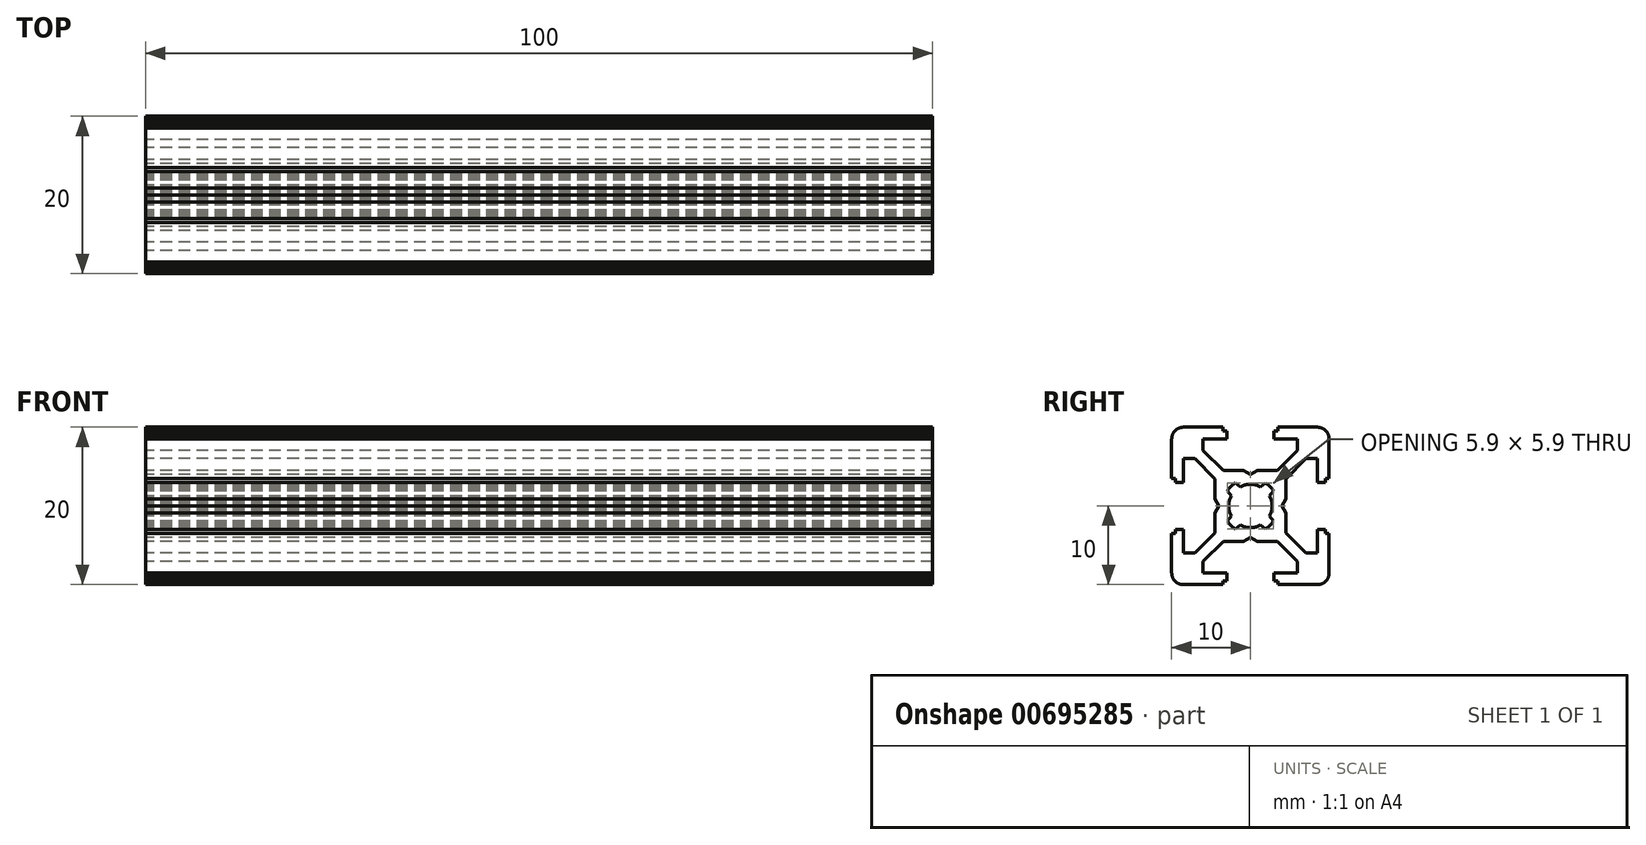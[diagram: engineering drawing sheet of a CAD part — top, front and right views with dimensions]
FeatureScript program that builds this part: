
annotation { "Feature Type Name" : "Feature", "Feature Type Description" : "" }
export const myFeature = defineFeature(function(context is Context, id is Id, definition is map)
    precondition{}
    {
        {
            var Q0;
            Q0=qCreatedBy(makeId("Right.planeOp"),FACE);
            var sketch = newSketch(context, id + "F0", { "sketchPlane" : qUnion([Q0])});
            skLineSegment(sketch, "E0", {"start": v(-10, -8.57) * mm, "end": v(-10, -8.5) * mm});
            skLineSegment(sketch, "E1", {"start": v(10, 8.5) * mm, "end": v(10, 8.57) * mm});
            skLineSegment(sketch, "E2", {"start": v(-2.74, -0.2) * mm, "end": v(-2.75, -0.07) * mm});
            skLineSegment(sketch, "E3", {"start": v(2.75, 0.07) * mm, "end": v(2.74, 0.2) * mm});
            skLineSegment(sketch, "E4", {"start": v(-10, -8.63) * mm, "end": v(-10, -8.57) * mm});
            skLineSegment(sketch, "E5", {"start": v(10, 8.57) * mm, "end": v(10, 8.63) * mm});
            skLineSegment(sketch, "E6", {"start": v(-2.73, -0.35) * mm, "end": v(-2.74, -0.2) * mm});
            skLineSegment(sketch, "E7", {"start": v(2.74, 0.2) * mm, "end": v(2.73, 0.35) * mm});
            skLineSegment(sketch, "E8", {"start": v(-9.99, -8.7) * mm, "end": v(-10, -8.63) * mm});
            skLineSegment(sketch, "E9", {"start": v(10, 8.63) * mm, "end": v(9.99, 8.7) * mm});
            skLineSegment(sketch, "E10", {"start": v(-2.7, -0.49) * mm, "end": v(-2.73, -0.35) * mm});
            skLineSegment(sketch, "E11", {"start": v(2.73, 0.35) * mm, "end": v(2.7, 0.49) * mm});
            skLineSegment(sketch, "E12", {"start": v(-9.98, -8.77) * mm, "end": v(-9.99, -8.7) * mm});
            skLineSegment(sketch, "E13", {"start": v(9.99, 8.7) * mm, "end": v(9.98, 8.77) * mm});
            skLineSegment(sketch, "E14", {"start": v(-9.96, -8.83) * mm, "end": v(-9.98, -8.77) * mm});
            skLineSegment(sketch, "E15", {"start": v(9.98, 8.77) * mm, "end": v(9.96, 8.83) * mm});
            skLineSegment(sketch, "E16", {"start": v(-2.68, -0.62) * mm, "end": v(-2.7, -0.49) * mm});
            skLineSegment(sketch, "E17", {"start": v(2.7, 0.49) * mm, "end": v(2.68, 0.62) * mm});
            skLineSegment(sketch, "E18", {"start": v(-9.95, -8.9) * mm, "end": v(-9.96, -8.83) * mm});
            skLineSegment(sketch, "E19", {"start": v(9.96, 8.83) * mm, "end": v(9.95, 8.9) * mm});
            skLineSegment(sketch, "E20", {"start": v(-2.64, -0.76) * mm, "end": v(-2.68, -0.62) * mm});
            skLineSegment(sketch, "E21", {"start": v(2.68, 0.62) * mm, "end": v(2.64, 0.76) * mm});
            skLineSegment(sketch, "E22", {"start": v(-9.93, -8.96) * mm, "end": v(-9.95, -8.9) * mm});
            skLineSegment(sketch, "E23", {"start": v(9.95, 8.9) * mm, "end": v(9.93, 8.96) * mm});
            skLineSegment(sketch, "E24", {"start": v(-2.6, -0.9) * mm, "end": v(-2.64, -0.76) * mm});
            skLineSegment(sketch, "E25", {"start": v(2.64, 0.76) * mm, "end": v(2.6, 0.9) * mm});
            skLineSegment(sketch, "E26", {"start": v(-9.9, -9.03) * mm, "end": v(-9.93, -8.96) * mm});
            skLineSegment(sketch, "E27", {"start": v(9.93, 8.96) * mm, "end": v(9.9, 9.03) * mm});
            skLineSegment(sketch, "E28", {"start": v(-2.55, -1.02) * mm, "end": v(-2.6, -0.9) * mm});
            skLineSegment(sketch, "E29", {"start": v(2.6, 0.9) * mm, "end": v(2.55, 1.02) * mm});
            skLineSegment(sketch, "E30", {"start": v(-9.88, -9.09) * mm, "end": v(-9.9, -9.03) * mm});
            skLineSegment(sketch, "E31", {"start": v(9.9, 9.03) * mm, "end": v(9.88, 9.09) * mm});
            skLineSegment(sketch, "E32", {"start": v(-2.5, -1.15) * mm, "end": v(-2.55, -1.02) * mm});
            skLineSegment(sketch, "E33", {"start": v(2.55, 1.02) * mm, "end": v(2.5, 1.15) * mm});
            skLineSegment(sketch, "E34", {"start": v(-9.85, -9.15) * mm, "end": v(-9.88, -9.09) * mm});
            skLineSegment(sketch, "E35", {"start": v(9.88, 9.09) * mm, "end": v(9.85, 9.15) * mm});
            skLineSegment(sketch, "E36", {"start": v(-2.44, -1.28) * mm, "end": v(-2.5, -1.15) * mm});
            skLineSegment(sketch, "E37", {"start": v(2.5, 1.15) * mm, "end": v(2.44, 1.28) * mm});
            skLineSegment(sketch, "E38", {"start": v(-9.82, -9.21) * mm, "end": v(-9.85, -9.15) * mm});
            skLineSegment(sketch, "E39", {"start": v(9.85, 9.15) * mm, "end": v(9.82, 9.21) * mm});
            skLineSegment(sketch, "E40", {"start": v(-9.79, -9.27) * mm, "end": v(-9.82, -9.21) * mm});
            skLineSegment(sketch, "E41", {"start": v(9.82, 9.21) * mm, "end": v(9.79, 9.27) * mm});
            skLineSegment(sketch, "E42", {"start": v(4.5, -0.87) * mm, "end": v(4, 0) * mm});
            skLineSegment(sketch, "E43", {"start": v(-4, 0) * mm, "end": v(-4.5, 0.87) * mm});
            skLineSegment(sketch, "E44", {"start": v(-9.75, -9.33) * mm, "end": v(-9.79, -9.27) * mm});
            skLineSegment(sketch, "E45", {"start": v(9.79, 9.27) * mm, "end": v(9.75, 9.33) * mm});
            skLineSegment(sketch, "E46", {"start": v(-2.87, -2) * mm, "end": v(-2.95, -1.89) * mm});
            skLineSegment(sketch, "E47", {"start": v(2.95, 1.89) * mm, "end": v(2.87, 2) * mm});
            skLineSegment(sketch, "E48", {"start": v(-9.71, -9.38) * mm, "end": v(-9.75, -9.33) * mm});
            skLineSegment(sketch, "E49", {"start": v(9.75, 9.33) * mm, "end": v(9.71, 9.38) * mm});
            skLineSegment(sketch, "E50", {"start": v(-2.8, -2.11) * mm, "end": v(-2.87, -2) * mm});
            skLineSegment(sketch, "E51", {"start": v(2.87, 2) * mm, "end": v(2.8, 2.11) * mm});
            skLineSegment(sketch, "E52", {"start": v(-9.67, -9.44) * mm, "end": v(-9.71, -9.38) * mm});
            skLineSegment(sketch, "E53", {"start": v(9.71, 9.38) * mm, "end": v(9.67, 9.44) * mm});
            skLineSegment(sketch, "E54", {"start": v(-2.7, -2.22) * mm, "end": v(-2.8, -2.11) * mm});
            skLineSegment(sketch, "E55", {"start": v(2.8, 2.11) * mm, "end": v(2.7, 2.22) * mm});
            skLineSegment(sketch, "E56", {"start": v(-9.63, -9.49) * mm, "end": v(-9.67, -9.44) * mm});
            skLineSegment(sketch, "E57", {"start": v(9.67, 9.44) * mm, "end": v(9.63, 9.49) * mm});
            skLineSegment(sketch, "E58", {"start": v(2.95, -1.89) * mm, "end": v(2.44, -1.28) * mm});
            skLineSegment(sketch, "E59", {"start": v(-2.44, 1.28) * mm, "end": v(-2.95, 1.89) * mm});
            skLineSegment(sketch, "E60", {"start": v(-2.62, -2.32) * mm, "end": v(-2.7, -2.22) * mm});
            skLineSegment(sketch, "E61", {"start": v(2.7, 2.22) * mm, "end": v(2.62, 2.32) * mm});
            skLineSegment(sketch, "E62", {"start": v(-9.58, -9.54) * mm, "end": v(-9.63, -9.49) * mm});
            skLineSegment(sketch, "E63", {"start": v(9.63, 9.49) * mm, "end": v(9.58, 9.54) * mm});
            skLineSegment(sketch, "E64", {"start": v(-2.52, -2.43) * mm, "end": v(-2.62, -2.32) * mm});
            skLineSegment(sketch, "E65", {"start": v(2.62, 2.32) * mm, "end": v(2.52, 2.43) * mm});
            skLineSegment(sketch, "E66", {"start": v(-2.43, -2.52) * mm, "end": v(-2.52, -2.43) * mm});
            skLineSegment(sketch, "E67", {"start": v(2.52, 2.43) * mm, "end": v(2.43, 2.52) * mm});
            skLineSegment(sketch, "E68", {"start": v(-9.54, -9.58) * mm, "end": v(-9.58, -9.54) * mm});
            skLineSegment(sketch, "E69", {"start": v(7.06, -6) * mm, "end": v(4.5, -3.44) * mm});
            skLineSegment(sketch, "E70", {"start": v(-4.5, 3.44) * mm, "end": v(-7.06, 6) * mm});
            skLineSegment(sketch, "E71", {"start": v(6, -7.06) * mm, "end": v(3.44, -4.5) * mm});
            skLineSegment(sketch, "E72", {"start": v(-3.44, 4.5) * mm, "end": v(-6, 7.06) * mm});
            skLineSegment(sketch, "E73", {"start": v(9.58, 9.54) * mm, "end": v(9.54, 9.58) * mm});
            skLineSegment(sketch, "E74", {"start": v(-2.32, -2.62) * mm, "end": v(-2.43, -2.52) * mm});
            skLineSegment(sketch, "E75", {"start": v(2.43, 2.52) * mm, "end": v(2.32, 2.62) * mm});
            skLineSegment(sketch, "E76", {"start": v(-9.49, -9.63) * mm, "end": v(-9.54, -9.58) * mm});
            skLineSegment(sketch, "E77", {"start": v(9.54, 9.58) * mm, "end": v(9.49, 9.63) * mm});
            skLineSegment(sketch, "E78", {"start": v(-2.22, -2.7) * mm, "end": v(-2.32, -2.62) * mm});
            skLineSegment(sketch, "E79", {"start": v(2.32, 2.62) * mm, "end": v(2.22, 2.7) * mm});
            skLineSegment(sketch, "E80", {"start": v(1.89, -2.95) * mm, "end": v(1.28, -2.44) * mm});
            skLineSegment(sketch, "E81", {"start": v(-1.28, 2.44) * mm, "end": v(-1.89, 2.95) * mm});
            skLineSegment(sketch, "E82", {"start": v(-9.44, -9.67) * mm, "end": v(-9.49, -9.63) * mm});
            skLineSegment(sketch, "E83", {"start": v(9.49, 9.63) * mm, "end": v(9.44, 9.67) * mm});
            skLineSegment(sketch, "E84", {"start": v(-2.11, -2.8) * mm, "end": v(-2.22, -2.7) * mm});
            skLineSegment(sketch, "E85", {"start": v(2.22, 2.7) * mm, "end": v(2.11, 2.8) * mm});
            skLineSegment(sketch, "E86", {"start": v(-9.38, -9.71) * mm, "end": v(-9.44, -9.67) * mm});
            skLineSegment(sketch, "E87", {"start": v(9.44, 9.67) * mm, "end": v(9.38, 9.71) * mm});
            skLineSegment(sketch, "E88", {"start": v(-2, -2.87) * mm, "end": v(-2.11, -2.8) * mm});
            skLineSegment(sketch, "E89", {"start": v(2.11, 2.8) * mm, "end": v(2, 2.87) * mm});
            skLineSegment(sketch, "E90", {"start": v(-9.33, -9.75) * mm, "end": v(-9.38, -9.71) * mm});
            skLineSegment(sketch, "E91", {"start": v(9.38, 9.71) * mm, "end": v(9.33, 9.75) * mm});
            skLineSegment(sketch, "E92", {"start": v(-1.89, -2.95) * mm, "end": v(-2, -2.87) * mm});
            skLineSegment(sketch, "E93", {"start": v(2, 2.87) * mm, "end": v(1.89, 2.95) * mm});
            skLineSegment(sketch, "E94", {"start": v(-9.27, -9.79) * mm, "end": v(-9.33, -9.75) * mm});
            skLineSegment(sketch, "E95", {"start": v(9.33, 9.75) * mm, "end": v(9.27, 9.79) * mm});
            skLineSegment(sketch, "E96", {"start": v(0.87, -4.5) * mm, "end": v(0, -4) * mm});
            skLineSegment(sketch, "E97", {"start": v(0, 4) * mm, "end": v(-0.87, 4.5) * mm});
            skLineSegment(sketch, "E98", {"start": v(-9.21, -9.82) * mm, "end": v(-9.27, -9.79) * mm});
            skLineSegment(sketch, "E99", {"start": v(9.27, 9.79) * mm, "end": v(9.21, 9.82) * mm});
            skLineSegment(sketch, "E100", {"start": v(-9.15, -9.85) * mm, "end": v(-9.21, -9.82) * mm});
            skLineSegment(sketch, "E101", {"start": v(9.21, 9.82) * mm, "end": v(9.15, 9.85) * mm});
            skLineSegment(sketch, "E102", {"start": v(-1.15, -2.5) * mm, "end": v(-1.28, -2.44) * mm});
            skLineSegment(sketch, "E103", {"start": v(1.28, 2.44) * mm, "end": v(1.15, 2.5) * mm});
            skLineSegment(sketch, "E104", {"start": v(-9.09, -9.88) * mm, "end": v(-9.15, -9.85) * mm});
            skLineSegment(sketch, "E105", {"start": v(9.15, 9.85) * mm, "end": v(9.09, 9.88) * mm});
            skLineSegment(sketch, "E106", {"start": v(-1.02, -2.55) * mm, "end": v(-1.15, -2.5) * mm});
            skLineSegment(sketch, "E107", {"start": v(1.15, 2.5) * mm, "end": v(1.02, 2.55) * mm});
            skLineSegment(sketch, "E108", {"start": v(-9.03, -9.9) * mm, "end": v(-9.09, -9.88) * mm});
            skLineSegment(sketch, "E109", {"start": v(9.09, 9.88) * mm, "end": v(9.03, 9.9) * mm});
            skLineSegment(sketch, "E110", {"start": v(-0.9, -2.6) * mm, "end": v(-1.02, -2.55) * mm});
            skLineSegment(sketch, "E111", {"start": v(1.02, 2.55) * mm, "end": v(0.9, 2.6) * mm});
            skLineSegment(sketch, "E112", {"start": v(-8.96, -9.93) * mm, "end": v(-9.03, -9.9) * mm});
            skLineSegment(sketch, "E113", {"start": v(9.03, 9.9) * mm, "end": v(8.96, 9.93) * mm});
            skLineSegment(sketch, "E114", {"start": v(-0.76, -2.64) * mm, "end": v(-0.9, -2.6) * mm});
            skLineSegment(sketch, "E115", {"start": v(0.9, 2.6) * mm, "end": v(0.76, 2.64) * mm});
            skLineSegment(sketch, "E116", {"start": v(-8.9, -9.95) * mm, "end": v(-8.96, -9.93) * mm});
            skLineSegment(sketch, "E117", {"start": v(8.96, 9.93) * mm, "end": v(8.9, 9.95) * mm});
            skLineSegment(sketch, "E118", {"start": v(-0.62, -2.68) * mm, "end": v(-0.76, -2.64) * mm});
            skLineSegment(sketch, "E119", {"start": v(0.76, 2.64) * mm, "end": v(0.62, 2.68) * mm});
            skLineSegment(sketch, "E120", {"start": v(-8.83, -9.96) * mm, "end": v(-8.9, -9.95) * mm});
            skLineSegment(sketch, "E121", {"start": v(8.9, 9.95) * mm, "end": v(8.83, 9.96) * mm});
            skLineSegment(sketch, "E122", {"start": v(-0.49, -2.7) * mm, "end": v(-0.62, -2.68) * mm});
            skLineSegment(sketch, "E123", {"start": v(0.62, 2.68) * mm, "end": v(0.49, 2.7) * mm});
            skLineSegment(sketch, "E124", {"start": v(-8.77, -9.98) * mm, "end": v(-8.83, -9.96) * mm});
            skLineSegment(sketch, "E125", {"start": v(8.83, 9.96) * mm, "end": v(8.77, 9.98) * mm});
            skLineSegment(sketch, "E126", {"start": v(-8.7, -9.99) * mm, "end": v(-8.77, -9.98) * mm});
            skLineSegment(sketch, "E127", {"start": v(8.77, 9.98) * mm, "end": v(8.7, 9.99) * mm});
            skLineSegment(sketch, "E128", {"start": v(-0.35, -2.73) * mm, "end": v(-0.49, -2.7) * mm});
            skLineSegment(sketch, "E129", {"start": v(0.49, 2.7) * mm, "end": v(0.35, 2.73) * mm});
            skLineSegment(sketch, "E130", {"start": v(-8.63, -10) * mm, "end": v(-8.7, -9.99) * mm});
            skLineSegment(sketch, "E131", {"start": v(8.7, 9.99) * mm, "end": v(8.63, 10) * mm});
            skLineSegment(sketch, "E132", {"start": v(-0.2, -2.74) * mm, "end": v(-0.35, -2.73) * mm});
            skLineSegment(sketch, "E133", {"start": v(0.35, 2.73) * mm, "end": v(0.2, 2.74) * mm});
            skLineSegment(sketch, "E134", {"start": v(-8.57, -10) * mm, "end": v(-8.63, -10) * mm});
            skLineSegment(sketch, "E135", {"start": v(8.63, 10) * mm, "end": v(8.57, 10) * mm});
            skLineSegment(sketch, "E136", {"start": v(-0.07, -2.75) * mm, "end": v(-0.2, -2.74) * mm});
            skLineSegment(sketch, "E137", {"start": v(0.2, 2.74) * mm, "end": v(0.07, 2.75) * mm});
            skLineSegment(sketch, "E138", {"start": v(-8.5, -10) * mm, "end": v(-8.57, -10) * mm});
            skLineSegment(sketch, "E139", {"start": v(8.57, 10) * mm, "end": v(8.5, 10) * mm});
            skLineSegment(sketch, "E140", {"start": v(-8.5, -10) * mm, "end": v(-3.5, -10) * mm});
            skLineSegment(sketch, "E141", {"start": v(3.5, -10) * mm, "end": v(8.5, -10) * mm});
            skLineSegment(sketch, "E142", {"start": v(-3.5, -9.5) * mm, "end": v(-3, -9.5) * mm});
            skLineSegment(sketch, "E143", {"start": v(3, -9.5) * mm, "end": v(3.5, -9.5) * mm});
            skLineSegment(sketch, "E144", {"start": v(-6, -8.5) * mm, "end": v(-3, -8.5) * mm});
            skLineSegment(sketch, "E145", {"start": v(3, -8.5) * mm, "end": v(6, -8.5) * mm});
            skLineSegment(sketch, "E146", {"start": v(-8.5, -6) * mm, "end": v(-7.06, -6) * mm});
            skLineSegment(sketch, "E147", {"start": v(7.06, -6) * mm, "end": v(8.5, -6) * mm});
            skLineSegment(sketch, "E148", {"start": v(-3.44, -4.5) * mm, "end": v(-0.87, -4.5) * mm});
            skLineSegment(sketch, "E149", {"start": v(0.87, -4.5) * mm, "end": v(3.44, -4.5) * mm});
            skLineSegment(sketch, "E150", {"start": v(-10, -3.5) * mm, "end": v(-9.5, -3.5) * mm});
            skLineSegment(sketch, "E151", {"start": v(9.5, -3.5) * mm, "end": v(10, -3.5) * mm});
            skLineSegment(sketch, "E152", {"start": v(-9.5, -3) * mm, "end": v(-8.5, -3) * mm});
            skLineSegment(sketch, "E153", {"start": v(8.5, -3) * mm, "end": v(9.5, -3) * mm});
            skLineSegment(sketch, "E154", {"start": v(-0.07, -2.75) * mm, "end": v(0.07, -2.75) * mm});
            skLineSegment(sketch, "E155", {"start": v(-0.07, 2.75) * mm, "end": v(0.07, 2.75) * mm});
            skLineSegment(sketch, "E156", {"start": v(8.5, 3) * mm, "end": v(9.5, 3) * mm});
            skLineSegment(sketch, "E157", {"start": v(-9.5, 3) * mm, "end": v(-8.5, 3) * mm});
            skLineSegment(sketch, "E158", {"start": v(9.5, 3.5) * mm, "end": v(10, 3.5) * mm});
            skLineSegment(sketch, "E159", {"start": v(-10, 3.5) * mm, "end": v(-9.5, 3.5) * mm});
            skLineSegment(sketch, "E160", {"start": v(0.87, 4.5) * mm, "end": v(3.44, 4.5) * mm});
            skLineSegment(sketch, "E161", {"start": v(-3.44, 4.5) * mm, "end": v(-0.87, 4.5) * mm});
            skLineSegment(sketch, "E162", {"start": v(7.06, 6) * mm, "end": v(8.5, 6) * mm});
            skLineSegment(sketch, "E163", {"start": v(-8.5, 6) * mm, "end": v(-7.06, 6) * mm});
            skLineSegment(sketch, "E164", {"start": v(3, 8.5) * mm, "end": v(6, 8.5) * mm});
            skLineSegment(sketch, "E165", {"start": v(-6, 8.5) * mm, "end": v(-3, 8.5) * mm});
            skLineSegment(sketch, "E166", {"start": v(3, 9.5) * mm, "end": v(3.5, 9.5) * mm});
            skLineSegment(sketch, "E167", {"start": v(-3.5, 9.5) * mm, "end": v(-3, 9.5) * mm});
            skLineSegment(sketch, "E168", {"start": v(3.5, 10) * mm, "end": v(8.5, 10) * mm});
            skLineSegment(sketch, "E169", {"start": v(-8.5, 10) * mm, "end": v(-3.5, 10) * mm});
            skLineSegment(sketch, "E170", {"start": v(8.5, -10) * mm, "end": v(8.57, -10) * mm});
            skLineSegment(sketch, "E171", {"start": v(-8.57, 10) * mm, "end": v(-8.5, 10) * mm});
            skLineSegment(sketch, "E172", {"start": v(0.07, -2.75) * mm, "end": v(0.2, -2.74) * mm});
            skLineSegment(sketch, "E173", {"start": v(-0.2, 2.74) * mm, "end": v(-0.07, 2.75) * mm});
            skLineSegment(sketch, "E174", {"start": v(8.57, -10) * mm, "end": v(8.63, -10) * mm});
            skLineSegment(sketch, "E175", {"start": v(-8.63, 10) * mm, "end": v(-8.57, 10) * mm});
            skLineSegment(sketch, "E176", {"start": v(0.2, -2.74) * mm, "end": v(0.35, -2.73) * mm});
            skLineSegment(sketch, "E177", {"start": v(-0.35, 2.73) * mm, "end": v(-0.2, 2.74) * mm});
            skLineSegment(sketch, "E178", {"start": v(8.63, -10) * mm, "end": v(8.7, -9.99) * mm});
            skLineSegment(sketch, "E179", {"start": v(-8.7, 9.99) * mm, "end": v(-8.63, 10) * mm});
            skLineSegment(sketch, "E180", {"start": v(0.35, -2.73) * mm, "end": v(0.49, -2.7) * mm});
            skLineSegment(sketch, "E181", {"start": v(-0.49, 2.7) * mm, "end": v(-0.35, 2.73) * mm});
            skLineSegment(sketch, "E182", {"start": v(8.7, -9.99) * mm, "end": v(8.77, -9.98) * mm});
            skLineSegment(sketch, "E183", {"start": v(-8.77, 9.98) * mm, "end": v(-8.7, 9.99) * mm});
            skLineSegment(sketch, "E184", {"start": v(8.77, -9.98) * mm, "end": v(8.83, -9.96) * mm});
            skLineSegment(sketch, "E185", {"start": v(-8.83, 9.96) * mm, "end": v(-8.77, 9.98) * mm});
            skLineSegment(sketch, "E186", {"start": v(0.49, -2.7) * mm, "end": v(0.62, -2.68) * mm});
            skLineSegment(sketch, "E187", {"start": v(-0.62, 2.68) * mm, "end": v(-0.49, 2.7) * mm});
            skLineSegment(sketch, "E188", {"start": v(8.83, -9.96) * mm, "end": v(8.9, -9.95) * mm});
            skLineSegment(sketch, "E189", {"start": v(-8.9, 9.95) * mm, "end": v(-8.83, 9.96) * mm});
            skLineSegment(sketch, "E190", {"start": v(0.62, -2.68) * mm, "end": v(0.76, -2.64) * mm});
            skLineSegment(sketch, "E191", {"start": v(-0.76, 2.64) * mm, "end": v(-0.62, 2.68) * mm});
            skLineSegment(sketch, "E192", {"start": v(8.9, -9.95) * mm, "end": v(8.96, -9.93) * mm});
            skLineSegment(sketch, "E193", {"start": v(-8.96, 9.93) * mm, "end": v(-8.9, 9.95) * mm});
            skLineSegment(sketch, "E194", {"start": v(0.76, -2.64) * mm, "end": v(0.9, -2.6) * mm});
            skLineSegment(sketch, "E195", {"start": v(-0.9, 2.6) * mm, "end": v(-0.76, 2.64) * mm});
            skLineSegment(sketch, "E196", {"start": v(8.96, -9.93) * mm, "end": v(9.03, -9.9) * mm});
            skLineSegment(sketch, "E197", {"start": v(-9.03, 9.9) * mm, "end": v(-8.96, 9.93) * mm});
            skLineSegment(sketch, "E198", {"start": v(0.9, -2.6) * mm, "end": v(1.02, -2.55) * mm});
            skLineSegment(sketch, "E199", {"start": v(-1.02, 2.55) * mm, "end": v(-0.9, 2.6) * mm});
            skLineSegment(sketch, "E200", {"start": v(9.03, -9.9) * mm, "end": v(9.09, -9.88) * mm});
            skLineSegment(sketch, "E201", {"start": v(-9.09, 9.88) * mm, "end": v(-9.03, 9.9) * mm});
            skLineSegment(sketch, "E202", {"start": v(1.02, -2.55) * mm, "end": v(1.15, -2.5) * mm});
            skLineSegment(sketch, "E203", {"start": v(-1.15, 2.5) * mm, "end": v(-1.02, 2.55) * mm});
            skLineSegment(sketch, "E204", {"start": v(9.09, -9.88) * mm, "end": v(9.15, -9.85) * mm});
            skLineSegment(sketch, "E205", {"start": v(-9.15, 9.85) * mm, "end": v(-9.09, 9.88) * mm});
            skLineSegment(sketch, "E206", {"start": v(1.15, -2.5) * mm, "end": v(1.28, -2.44) * mm});
            skLineSegment(sketch, "E207", {"start": v(-1.28, 2.44) * mm, "end": v(-1.15, 2.5) * mm});
            skLineSegment(sketch, "E208", {"start": v(9.15, -9.85) * mm, "end": v(9.21, -9.82) * mm});
            skLineSegment(sketch, "E209", {"start": v(-9.21, 9.82) * mm, "end": v(-9.15, 9.85) * mm});
            skLineSegment(sketch, "E210", {"start": v(9.21, -9.82) * mm, "end": v(9.27, -9.79) * mm});
            skLineSegment(sketch, "E211", {"start": v(-9.27, 9.79) * mm, "end": v(-9.21, 9.82) * mm});
            skLineSegment(sketch, "E212", {"start": v(-0.87, -4.5) * mm, "end": v(0, -4) * mm});
            skLineSegment(sketch, "E213", {"start": v(0, 4) * mm, "end": v(0.87, 4.5) * mm});
            skLineSegment(sketch, "E214", {"start": v(9.27, -9.79) * mm, "end": v(9.33, -9.75) * mm});
            skLineSegment(sketch, "E215", {"start": v(-9.33, 9.75) * mm, "end": v(-9.27, 9.79) * mm});
            skLineSegment(sketch, "E216", {"start": v(1.89, -2.95) * mm, "end": v(2, -2.87) * mm});
            skLineSegment(sketch, "E217", {"start": v(-2, 2.87) * mm, "end": v(-1.89, 2.95) * mm});
            skLineSegment(sketch, "E218", {"start": v(9.33, -9.75) * mm, "end": v(9.38, -9.71) * mm});
            skLineSegment(sketch, "E219", {"start": v(-9.38, 9.71) * mm, "end": v(-9.33, 9.75) * mm});
            skLineSegment(sketch, "E220", {"start": v(2, -2.87) * mm, "end": v(2.11, -2.8) * mm});
            skLineSegment(sketch, "E221", {"start": v(-2.11, 2.8) * mm, "end": v(-2, 2.87) * mm});
            skLineSegment(sketch, "E222", {"start": v(9.38, -9.71) * mm, "end": v(9.44, -9.67) * mm});
            skLineSegment(sketch, "E223", {"start": v(-9.44, 9.67) * mm, "end": v(-9.38, 9.71) * mm});
            skLineSegment(sketch, "E224", {"start": v(2.11, -2.8) * mm, "end": v(2.22, -2.7) * mm});
            skLineSegment(sketch, "E225", {"start": v(-2.22, 2.7) * mm, "end": v(-2.11, 2.8) * mm});
            skLineSegment(sketch, "E226", {"start": v(9.44, -9.67) * mm, "end": v(9.49, -9.63) * mm});
            skLineSegment(sketch, "E227", {"start": v(-9.49, 9.63) * mm, "end": v(-9.44, 9.67) * mm});
            skLineSegment(sketch, "E228", {"start": v(-1.89, -2.95) * mm, "end": v(-1.28, -2.44) * mm});
            skLineSegment(sketch, "E229", {"start": v(1.28, 2.44) * mm, "end": v(1.89, 2.95) * mm});
            skLineSegment(sketch, "E230", {"start": v(2.22, -2.7) * mm, "end": v(2.32, -2.62) * mm});
            skLineSegment(sketch, "E231", {"start": v(-2.32, 2.62) * mm, "end": v(-2.22, 2.7) * mm});
            skLineSegment(sketch, "E232", {"start": v(9.49, -9.63) * mm, "end": v(9.54, -9.58) * mm});
            skLineSegment(sketch, "E233", {"start": v(-9.54, 9.58) * mm, "end": v(-9.49, 9.63) * mm});
            skLineSegment(sketch, "E234", {"start": v(2.32, -2.62) * mm, "end": v(2.43, -2.52) * mm});
            skLineSegment(sketch, "E235", {"start": v(-2.43, 2.52) * mm, "end": v(-2.32, 2.62) * mm});
            skLineSegment(sketch, "E236", {"start": v(9.54, -9.58) * mm, "end": v(9.58, -9.54) * mm});
            skLineSegment(sketch, "E237", {"start": v(-7.06, -6) * mm, "end": v(-4.5, -3.44) * mm});
            skLineSegment(sketch, "E238", {"start": v(4.5, 3.44) * mm, "end": v(7.06, 6) * mm});
            skLineSegment(sketch, "E239", {"start": v(-6, -7.06) * mm, "end": v(-3.44, -4.5) * mm});
            skLineSegment(sketch, "E240", {"start": v(3.44, 4.5) * mm, "end": v(6, 7.06) * mm});
            skLineSegment(sketch, "E241", {"start": v(-9.58, 9.54) * mm, "end": v(-9.54, 9.58) * mm});
            skLineSegment(sketch, "E242", {"start": v(2.43, -2.52) * mm, "end": v(2.52, -2.43) * mm});
            skLineSegment(sketch, "E243", {"start": v(-2.52, 2.43) * mm, "end": v(-2.43, 2.52) * mm});
            skLineSegment(sketch, "E244", {"start": v(2.52, -2.43) * mm, "end": v(2.62, -2.32) * mm});
            skLineSegment(sketch, "E245", {"start": v(-2.62, 2.32) * mm, "end": v(-2.52, 2.43) * mm});
            skLineSegment(sketch, "E246", {"start": v(9.58, -9.54) * mm, "end": v(9.63, -9.49) * mm});
            skLineSegment(sketch, "E247", {"start": v(-9.63, 9.49) * mm, "end": v(-9.58, 9.54) * mm});
            skLineSegment(sketch, "E248", {"start": v(2.62, -2.32) * mm, "end": v(2.7, -2.22) * mm});
            skLineSegment(sketch, "E249", {"start": v(-2.7, 2.22) * mm, "end": v(-2.62, 2.32) * mm});
            skLineSegment(sketch, "E250", {"start": v(-2.95, -1.89) * mm, "end": v(-2.44, -1.28) * mm});
            skLineSegment(sketch, "E251", {"start": v(2.44, 1.28) * mm, "end": v(2.95, 1.89) * mm});
            skLineSegment(sketch, "E252", {"start": v(9.63, -9.49) * mm, "end": v(9.67, -9.44) * mm});
            skLineSegment(sketch, "E253", {"start": v(-9.67, 9.44) * mm, "end": v(-9.63, 9.49) * mm});
            skLineSegment(sketch, "E254", {"start": v(2.7, -2.22) * mm, "end": v(2.8, -2.11) * mm});
            skLineSegment(sketch, "E255", {"start": v(-2.8, 2.11) * mm, "end": v(-2.7, 2.22) * mm});
            skLineSegment(sketch, "E256", {"start": v(9.67, -9.44) * mm, "end": v(9.71, -9.38) * mm});
            skLineSegment(sketch, "E257", {"start": v(-9.71, 9.38) * mm, "end": v(-9.67, 9.44) * mm});
            skLineSegment(sketch, "E258", {"start": v(2.8, -2.11) * mm, "end": v(2.87, -2) * mm});
            skLineSegment(sketch, "E259", {"start": v(-2.87, 2) * mm, "end": v(-2.8, 2.11) * mm});
            skLineSegment(sketch, "E260", {"start": v(9.71, -9.38) * mm, "end": v(9.75, -9.33) * mm});
            skLineSegment(sketch, "E261", {"start": v(-9.75, 9.33) * mm, "end": v(-9.71, 9.38) * mm});
            skLineSegment(sketch, "E262", {"start": v(2.87, -2) * mm, "end": v(2.95, -1.89) * mm});
            skLineSegment(sketch, "E263", {"start": v(-2.95, 1.89) * mm, "end": v(-2.87, 2) * mm});
            skLineSegment(sketch, "E264", {"start": v(9.75, -9.33) * mm, "end": v(9.79, -9.27) * mm});
            skLineSegment(sketch, "E265", {"start": v(-9.79, 9.27) * mm, "end": v(-9.75, 9.33) * mm});
            skLineSegment(sketch, "E266", {"start": v(-4.5, -0.87) * mm, "end": v(-4, 0) * mm});
            skLineSegment(sketch, "E267", {"start": v(4, 0) * mm, "end": v(4.5, 0.87) * mm});
            skLineSegment(sketch, "E268", {"start": v(9.79, -9.27) * mm, "end": v(9.82, -9.21) * mm});
            skLineSegment(sketch, "E269", {"start": v(-9.82, 9.21) * mm, "end": v(-9.79, 9.27) * mm});
            skLineSegment(sketch, "E270", {"start": v(9.82, -9.21) * mm, "end": v(9.85, -9.15) * mm});
            skLineSegment(sketch, "E271", {"start": v(-9.85, 9.15) * mm, "end": v(-9.82, 9.21) * mm});
            skLineSegment(sketch, "E272", {"start": v(2.44, -1.28) * mm, "end": v(2.5, -1.15) * mm});
            skLineSegment(sketch, "E273", {"start": v(-2.5, 1.15) * mm, "end": v(-2.44, 1.28) * mm});
            skLineSegment(sketch, "E274", {"start": v(9.85, -9.15) * mm, "end": v(9.88, -9.09) * mm});
            skLineSegment(sketch, "E275", {"start": v(-9.88, 9.09) * mm, "end": v(-9.85, 9.15) * mm});
            skLineSegment(sketch, "E276", {"start": v(2.5, -1.15) * mm, "end": v(2.55, -1.02) * mm});
            skLineSegment(sketch, "E277", {"start": v(-2.55, 1.02) * mm, "end": v(-2.5, 1.15) * mm});
            skLineSegment(sketch, "E278", {"start": v(9.88, -9.09) * mm, "end": v(9.9, -9.03) * mm});
            skLineSegment(sketch, "E279", {"start": v(-9.9, 9.03) * mm, "end": v(-9.88, 9.09) * mm});
            skLineSegment(sketch, "E280", {"start": v(2.55, -1.02) * mm, "end": v(2.6, -0.9) * mm});
            skLineSegment(sketch, "E281", {"start": v(-2.6, 0.9) * mm, "end": v(-2.55, 1.02) * mm});
            skLineSegment(sketch, "E282", {"start": v(9.9, -9.03) * mm, "end": v(9.93, -8.96) * mm});
            skLineSegment(sketch, "E283", {"start": v(-9.93, 8.96) * mm, "end": v(-9.9, 9.03) * mm});
            skLineSegment(sketch, "E284", {"start": v(2.6, -0.9) * mm, "end": v(2.64, -0.76) * mm});
            skLineSegment(sketch, "E285", {"start": v(-2.64, 0.76) * mm, "end": v(-2.6, 0.9) * mm});
            skLineSegment(sketch, "E286", {"start": v(9.93, -8.96) * mm, "end": v(9.95, -8.9) * mm});
            skLineSegment(sketch, "E287", {"start": v(-9.95, 8.9) * mm, "end": v(-9.93, 8.96) * mm});
            skLineSegment(sketch, "E288", {"start": v(2.64, -0.76) * mm, "end": v(2.68, -0.62) * mm});
            skLineSegment(sketch, "E289", {"start": v(-2.68, 0.62) * mm, "end": v(-2.64, 0.76) * mm});
            skLineSegment(sketch, "E290", {"start": v(9.95, -8.9) * mm, "end": v(9.96, -8.83) * mm});
            skLineSegment(sketch, "E291", {"start": v(-9.96, 8.83) * mm, "end": v(-9.95, 8.9) * mm});
            skLineSegment(sketch, "E292", {"start": v(2.68, -0.62) * mm, "end": v(2.7, -0.49) * mm});
            skLineSegment(sketch, "E293", {"start": v(-2.7, 0.49) * mm, "end": v(-2.68, 0.62) * mm});
            skLineSegment(sketch, "E294", {"start": v(9.96, -8.83) * mm, "end": v(9.98, -8.77) * mm});
            skLineSegment(sketch, "E295", {"start": v(-9.98, 8.77) * mm, "end": v(-9.96, 8.83) * mm});
            skLineSegment(sketch, "E296", {"start": v(9.98, -8.77) * mm, "end": v(9.99, -8.7) * mm});
            skLineSegment(sketch, "E297", {"start": v(-9.99, 8.7) * mm, "end": v(-9.98, 8.77) * mm});
            skLineSegment(sketch, "E298", {"start": v(2.7, -0.49) * mm, "end": v(2.73, -0.35) * mm});
            skLineSegment(sketch, "E299", {"start": v(-2.73, 0.35) * mm, "end": v(-2.7, 0.49) * mm});
            skLineSegment(sketch, "E300", {"start": v(9.99, -8.7) * mm, "end": v(10, -8.63) * mm});
            skLineSegment(sketch, "E301", {"start": v(-10, 8.63) * mm, "end": v(-9.99, 8.7) * mm});
            skLineSegment(sketch, "E302", {"start": v(2.73, -0.35) * mm, "end": v(2.74, -0.2) * mm});
            skLineSegment(sketch, "E303", {"start": v(-2.74, 0.2) * mm, "end": v(-2.73, 0.35) * mm});
            skLineSegment(sketch, "E304", {"start": v(10, -8.63) * mm, "end": v(10, -8.57) * mm});
            skLineSegment(sketch, "E305", {"start": v(-10, 8.57) * mm, "end": v(-10, 8.63) * mm});
            skLineSegment(sketch, "E306", {"start": v(2.74, -0.2) * mm, "end": v(2.75, -0.07) * mm});
            skLineSegment(sketch, "E307", {"start": v(-2.75, 0.07) * mm, "end": v(-2.74, 0.2) * mm});
            skLineSegment(sketch, "E308", {"start": v(10, -8.57) * mm, "end": v(10, -8.5) * mm});
            skLineSegment(sketch, "E309", {"start": v(-10, 8.5) * mm, "end": v(-10, 8.57) * mm});
            skLineSegment(sketch, "E310", {"start": v(-10, 3.5) * mm, "end": v(-10, 8.5) * mm});
            skLineSegment(sketch, "E311", {"start": v(-10, -8.5) * mm, "end": v(-10, -3.5) * mm});
            skLineSegment(sketch, "E312", {"start": v(-9.5, 3) * mm, "end": v(-9.5, 3.5) * mm});
            skLineSegment(sketch, "E313", {"start": v(-9.5, -3.5) * mm, "end": v(-9.5, -3) * mm});
            skLineSegment(sketch, "E314", {"start": v(-8.5, 3) * mm, "end": v(-8.5, 6) * mm});
            skLineSegment(sketch, "E315", {"start": v(-8.5, -6) * mm, "end": v(-8.5, -3) * mm});
            skLineSegment(sketch, "E316", {"start": v(-6, 7.06) * mm, "end": v(-6, 8.5) * mm});
            skLineSegment(sketch, "E317", {"start": v(-6, -8.5) * mm, "end": v(-6, -7.06) * mm});
            skLineSegment(sketch, "E318", {"start": v(-4.5, 0.87) * mm, "end": v(-4.5, 3.44) * mm});
            skLineSegment(sketch, "E319", {"start": v(-4.5, -3.44) * mm, "end": v(-4.5, -0.87) * mm});
            skLineSegment(sketch, "E320", {"start": v(-3.5, 9.5) * mm, "end": v(-3.5, 10) * mm});
            skLineSegment(sketch, "E321", {"start": v(-3.5, -10) * mm, "end": v(-3.5, -9.5) * mm});
            skLineSegment(sketch, "E322", {"start": v(-3, 8.5) * mm, "end": v(-3, 9.5) * mm});
            skLineSegment(sketch, "E323", {"start": v(-3, -9.5) * mm, "end": v(-3, -8.5) * mm});
            skLineSegment(sketch, "E324", {"start": v(-2.75, -0.07) * mm, "end": v(-2.75, 0.07) * mm});
            skLineSegment(sketch, "E325", {"start": v(2.75, -0.07) * mm, "end": v(2.75, 0.07) * mm});
            skLineSegment(sketch, "E326", {"start": v(3, 8.5) * mm, "end": v(3, 9.5) * mm});
            skLineSegment(sketch, "E327", {"start": v(3, -9.5) * mm, "end": v(3, -8.5) * mm});
            skLineSegment(sketch, "E328", {"start": v(3.5, 9.5) * mm, "end": v(3.5, 10) * mm});
            skLineSegment(sketch, "E329", {"start": v(3.5, -10) * mm, "end": v(3.5, -9.5) * mm});
            skLineSegment(sketch, "E330", {"start": v(4.5, -3.44) * mm, "end": v(4.5, -0.87) * mm});
            skLineSegment(sketch, "E331", {"start": v(4.5, 0.87) * mm, "end": v(4.5, 3.44) * mm});
            skLineSegment(sketch, "E332", {"start": v(6, 7.06) * mm, "end": v(6, 8.5) * mm});
            skLineSegment(sketch, "E333", {"start": v(6, -8.5) * mm, "end": v(6, -7.06) * mm});
            skLineSegment(sketch, "E334", {"start": v(8.5, 3) * mm, "end": v(8.5, 6) * mm});
            skLineSegment(sketch, "E335", {"start": v(8.5, -6) * mm, "end": v(8.5, -3) * mm});
            skLineSegment(sketch, "E336", {"start": v(9.5, 3) * mm, "end": v(9.5, 3.5) * mm});
            skLineSegment(sketch, "E337", {"start": v(9.5, -3.5) * mm, "end": v(9.5, -3) * mm});
            skLineSegment(sketch, "E338", {"start": v(10, 3.5) * mm, "end": v(10, 8.5) * mm});
            skLineSegment(sketch, "E339", {"start": v(10, -8.5) * mm, "end": v(10, -3.5) * mm});
            skSolve(sketch);
        }
        {
            var Q0;
            Q0 = qSketchRegion(id + "F0", true);
            extrude(context, id + "F1", {"entities" : qUnion([Q0]), "depth" : 100 * mm, "offsetDistance" : 25 * mm});
        }
    });
